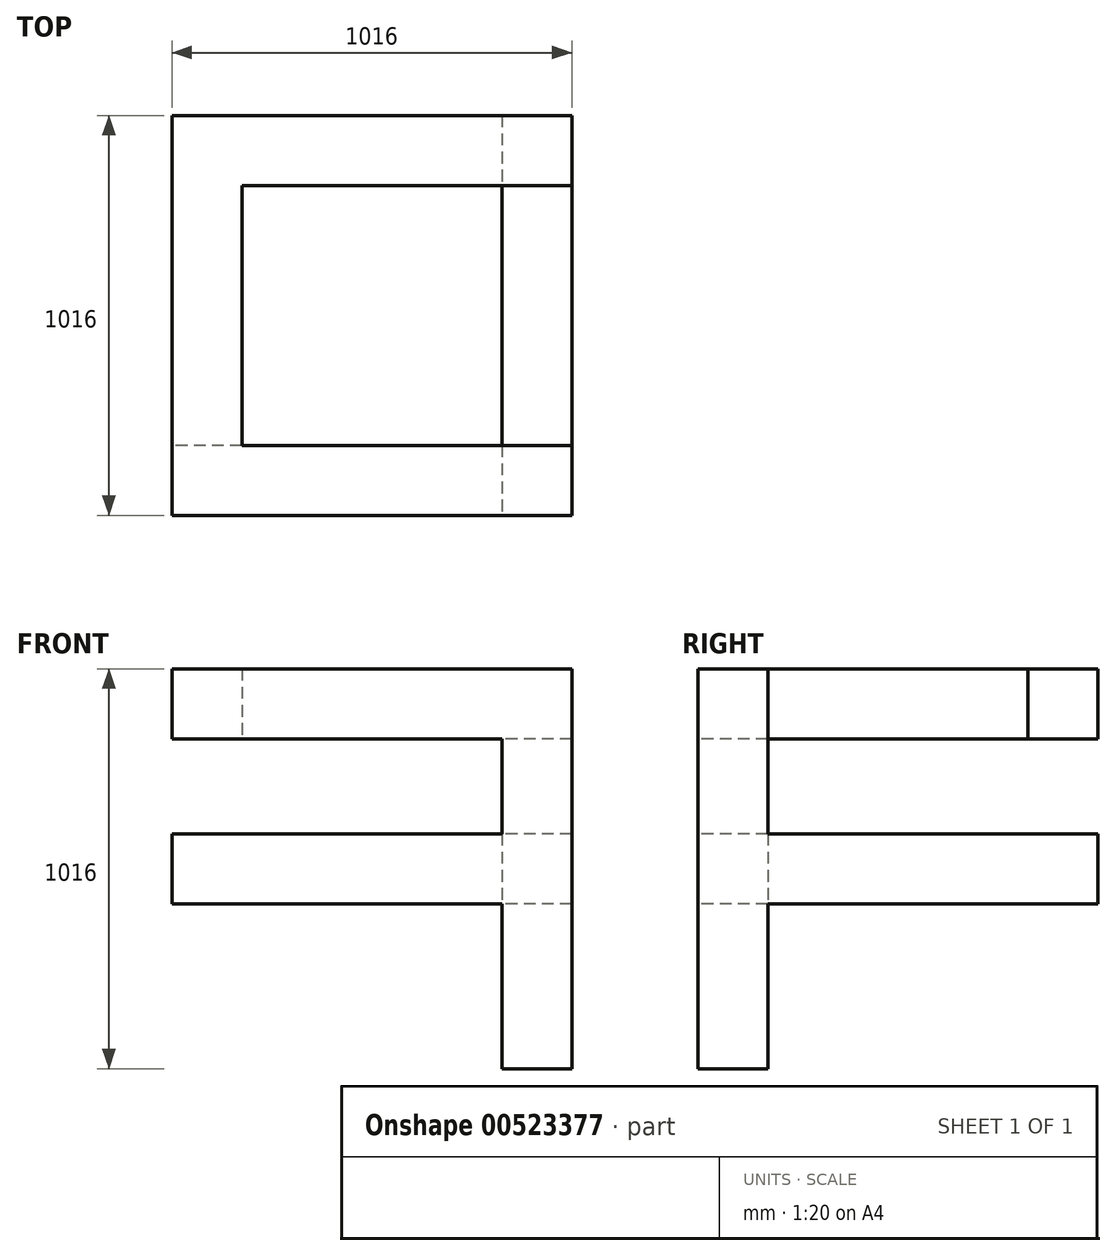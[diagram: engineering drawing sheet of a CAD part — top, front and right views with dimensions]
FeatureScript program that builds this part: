
annotation { "Feature Type Name" : "Feature", "Feature Type Description" : "" }
export const myFeature = defineFeature(function(context is Context, id is Id, definition is map)
    precondition{}
    {
        {
            var Q0;
            Q0=qCreatedBy(makeId("Top.planeOp"),FACE);
            var sketch = newSketch(context, id + "F0", { "sketchPlane" : qUnion([Q0])});
            skLineSegment(sketch, "E0.bottom", {"start": v(508, 508) * mm, "end": v(-508, 508) * mm});
            skLineSegment(sketch, "E0.top", {"start": v(508, -508) * mm, "end": v(-508, -508) * mm});
            skLineSegment(sketch, "E0.left", {"start": v(508, 508) * mm, "end": v(508, -508) * mm});
            skLineSegment(sketch, "E0.right", {"start": v(-508, 508) * mm, "end": v(-508, -508) * mm});
            skPoint(sketch, "E0.middle", {"position": v(0, 0) * mm});
            skLineSegment(sketch, "E1", {"start": v(508, 330.2) * mm, "end": v(-330.2, 330.2) * mm});
            skLineSegment(sketch, "E2", {"start": v(-330.2, 330.2) * mm, "end": v(-330.2, -330.2) * mm});
            skLineSegment(sketch, "E3", {"start": v(-330.2, -330.2) * mm, "end": v(508, -330.2) * mm});
            skSolve(sketch);
        }
        {
            var Q0;
            {var subQ3=sQuery(id+"F0.wireOp",EDGE,"E0.bottom");Q0=makeQuery(id+"F0.imprint","IMPRINT",FACE,{"disambiguationData":[TD([[makeQuery(id+"F0.imprint","IMPRINT",EDGE,{"derivedFrom":subQ3}),1.0]])]});}
            extrude(context, id + "F1", {"entities" : qUnion([Q0]), "depth" : 177.8 * mm, "offsetDistance" : 25.4 * mm});
        }
        {
            var Q0;
            Q0=makeQuery(id+"F1.opExtrude","SWEPT_FACE",FACE,{"disambiguationData":[OSD([sQuery(id+"F0.wireOp",EDGE,"E0.top")])]});
            var sketch = newSketch(context, id + "F2", { "sketchPlane" : qUnion([Q0])});
            skLineSegment(sketch, "E4.bottom", {"start": v(508, 177.8) * mm, "end": v(330.2, 177.8) * mm});
            skLineSegment(sketch, "E4.top", {"start": v(508, -838.2) * mm, "end": v(330.2, -838.2) * mm});
            skLineSegment(sketch, "E4.left", {"start": v(508, 177.8) * mm, "end": v(508, -838.2) * mm});
            skLineSegment(sketch, "E4.right", {"start": v(330.2, 177.8) * mm, "end": v(330.2, -838.2) * mm});
            skLineSegment(sketch, "E5.bottom", {"start": v(508, -241.3) * mm, "end": v(-508, -241.3) * mm});
            skLineSegment(sketch, "E5.top", {"start": v(508, -419.1) * mm, "end": v(-508, -419.1) * mm});
            skLineSegment(sketch, "E5.left", {"start": v(508, -241.3) * mm, "end": v(508, -419.1) * mm});
            skLineSegment(sketch, "E5.right", {"start": v(-508, -241.3) * mm, "end": v(-508, -419.1) * mm});
            skSolve(sketch);
        }
        {
            var Q0;
            {var subQ3=sQuery(id+"F2.wireOp",EDGE,"E5.bottom");var subQ5=sQuery(id+"F2.wireOp",EDGE,"E4.right");var subQ6=makeQuery(id+"F2.imprint","INTERSECT",VERTEX,{"derivedFrom":[subQ5,subQ3]});Q0=makeQuery(id+"F2.imprint","IMPRINT",FACE,{"disambiguationData":[TD([[makeQuery(id+"F2.imprint","IMPRINT",EDGE,{"disambiguationData":[TD([[subQ6,1.0]])],"derivedFrom":subQ5}),1.0]])]});}
            var Q1;
            {var subQ5=sQuery(id+"F2.wireOp",EDGE,"E5.left");Q1=makeQuery(id+"F2.imprint","IMPRINT",FACE,{"disambiguationData":[TD([[makeQuery(id+"F2.imprint","IMPRINT",EDGE,{"derivedFrom":subQ5}),-1.0]])]});}
            var Q2;
            {var subQ0=sQuery(id+"F2.wireOp",EDGE,"E4.top");Q2=makeQuery(id+"F2.imprint","IMPRINT",FACE,{"disambiguationData":[TD([[makeQuery(id+"F2.imprint","IMPRINT",EDGE,{"derivedFrom":subQ0}),-1.0]])]});}
            var Q3;
            {var subQ5=sQuery(id+"F2.wireOp",EDGE,"E5.right");Q3=makeQuery(id+"F2.imprint","IMPRINT",FACE,{"disambiguationData":[TD([[makeQuery(id+"F2.imprint","IMPRINT",EDGE,{"derivedFrom":subQ5}),1.0]])]});}
            extrude(context, id + "F3", {"entities" : qUnion([Q0, Q1, Q2, Q3]), "operationType" : NewBodyOperationType.ADD, "oppositeDirection" : true, "depth" : 177.8 * mm, "offsetDistance" : 25.4 * mm});
        }
        {
            var Q0;
            {var subQ0=sQuery(id+"F0.wireOp",EDGE,"E0.left");Q0=makeQuery(id+"F3.boolean.opBoolean","MERGE",FACE,{"derivedFrom":[makeQuery(id+"F1.opExtrude","SWEPT_FACE",FACE,{"disambiguationData":[OSD([subQ0]),TDD([makeQuery(id+"F0.imprint","IMPRINT",EDGE,{"disambiguationData":[TD([[makeQuery(id+"F0.imprint","INTERSECT",VERTEX,{"derivedFrom":[sQuery(id+"F0.wireOp",EDGE,"E0.top"),subQ0]}),1.0]])],"derivedFrom":subQ0})])]}),makeQuery(id+"F3.opExtrude","SWEPT_FACE",FACE,{"disambiguationData":[OSD([sQuery(id+"F2.wireOp",EDGE,"E4.left"),sQuery(id+"F2.wireOp",EDGE,"E5.left")])]})]});}
            var sketch = newSketch(context, id + "F4", { "sketchPlane" : qUnion([Q0])});
            skLineSegment(sketch, "E6.bottom", {"start": v(-508, -241.3) * mm, "end": v(508, -241.3) * mm});
            skLineSegment(sketch, "E6.top", {"start": v(-508, -419.1) * mm, "end": v(508, -419.1) * mm});
            skLineSegment(sketch, "E6.left", {"start": v(-508, -241.3) * mm, "end": v(-508, -419.1) * mm});
            skLineSegment(sketch, "E6.right", {"start": v(508, -241.3) * mm, "end": v(508, -419.1) * mm});
            skSolve(sketch);
        }
        {
            var Q0;
            {var subQ0=sQuery(id+"F4.wireOp",EDGE,"E6.right");Q0=makeQuery(id+"F4.imprint","IMPRINT",FACE,{"disambiguationData":[TD([[makeQuery(id+"F4.imprint","IMPRINT",EDGE,{"derivedFrom":subQ0}),-1.0]])]});}
            extrude(context, id + "F5", {"entities" : qUnion([Q0]), "operationType" : NewBodyOperationType.ADD, "oppositeDirection" : true, "depth" : 177.8 * mm, "offsetDistance" : 25.4 * mm});
        }
    });
